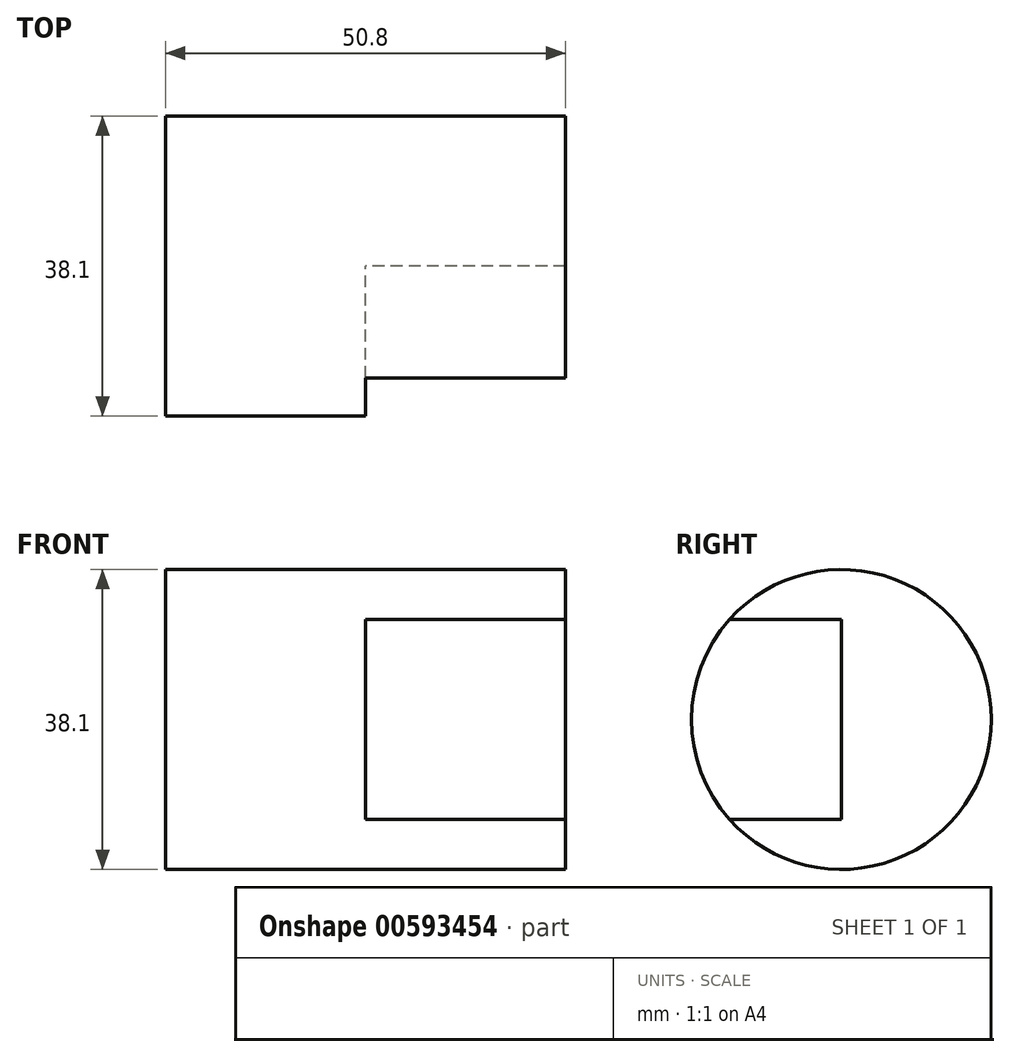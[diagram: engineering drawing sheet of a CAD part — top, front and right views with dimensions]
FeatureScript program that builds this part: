
annotation { "Feature Type Name" : "Feature", "Feature Type Description" : "" }
export const myFeature = defineFeature(function(context is Context, id is Id, definition is map)
    precondition{}
    {
        {
            var Q0;
            Q0=qCreatedBy(makeId("Right.planeOp"),FACE);
            var sketch = newSketch(context, id + "F0", { "sketchPlane" : qUnion([Q0])});
            skCircle(sketch, "E0", {"center": v(0, 0) * mm, "radius": 19.05 * mm});
            skSolve(sketch);
        }
        {
            var Q0;
            Q0 = qSketchRegion(id + "F0", true);
            extrude(context, id + "F1", {"entities" : qUnion([Q0]), "depth" : 50.8 * mm, "offsetDistance" : 25.4 * mm});
        }
        {
            var Q0;
            Q0=makeQuery(id+"F1.opExtrude","CAP_FACE",FACE,{"disambiguationData":[OSD([sQuery(id+"F0.wireOp",EDGE,"E0")])],"isStart":false});
            cPlane(context, id + "F2", {"entities" : qUnion([Q0]), "cplaneType" : CPlaneType.OFFSET, "offset" : 25.4 * mm, "oppositeDirection" : true, "width" : 152.4 * mm, "height" : 152.4 * mm});
        }
        {
            var Q0;
            Q0=qCreatedBy(id+"F2.planeOp",FACE);
            var sketch = newSketch(context, id + "F3", { "sketchPlane" : qUnion([Q0])});
            skLineSegment(sketch, "E1", {"start": v(-14.2, 12.7) * mm, "end": v(0, 12.7) * mm});
            skLineSegment(sketch, "E2", {"start": v(0, 12.7) * mm, "end": v(0, -12.7) * mm});
            skLineSegment(sketch, "E3", {"start": v(0, -12.7) * mm, "end": v(-14.2, -12.7) * mm});
            skArc(sketch, "E4", {"start": v(-14.2, 12.7) * mm, "mid": v(-19.05, 0) * mm, "end": v(-14.2, -12.7) * mm});
            skSolve(sketch);
        }
        {
            var Q0;
            Q0 = qSketchRegion(id + "F3", true);
            extrude(context, id + "F4", {"entities" : qUnion([Q0]), "operationType" : NewBodyOperationType.REMOVE, "depth" : 25.4 * mm, "offsetDistance" : 25.4 * mm});
        }
    });
